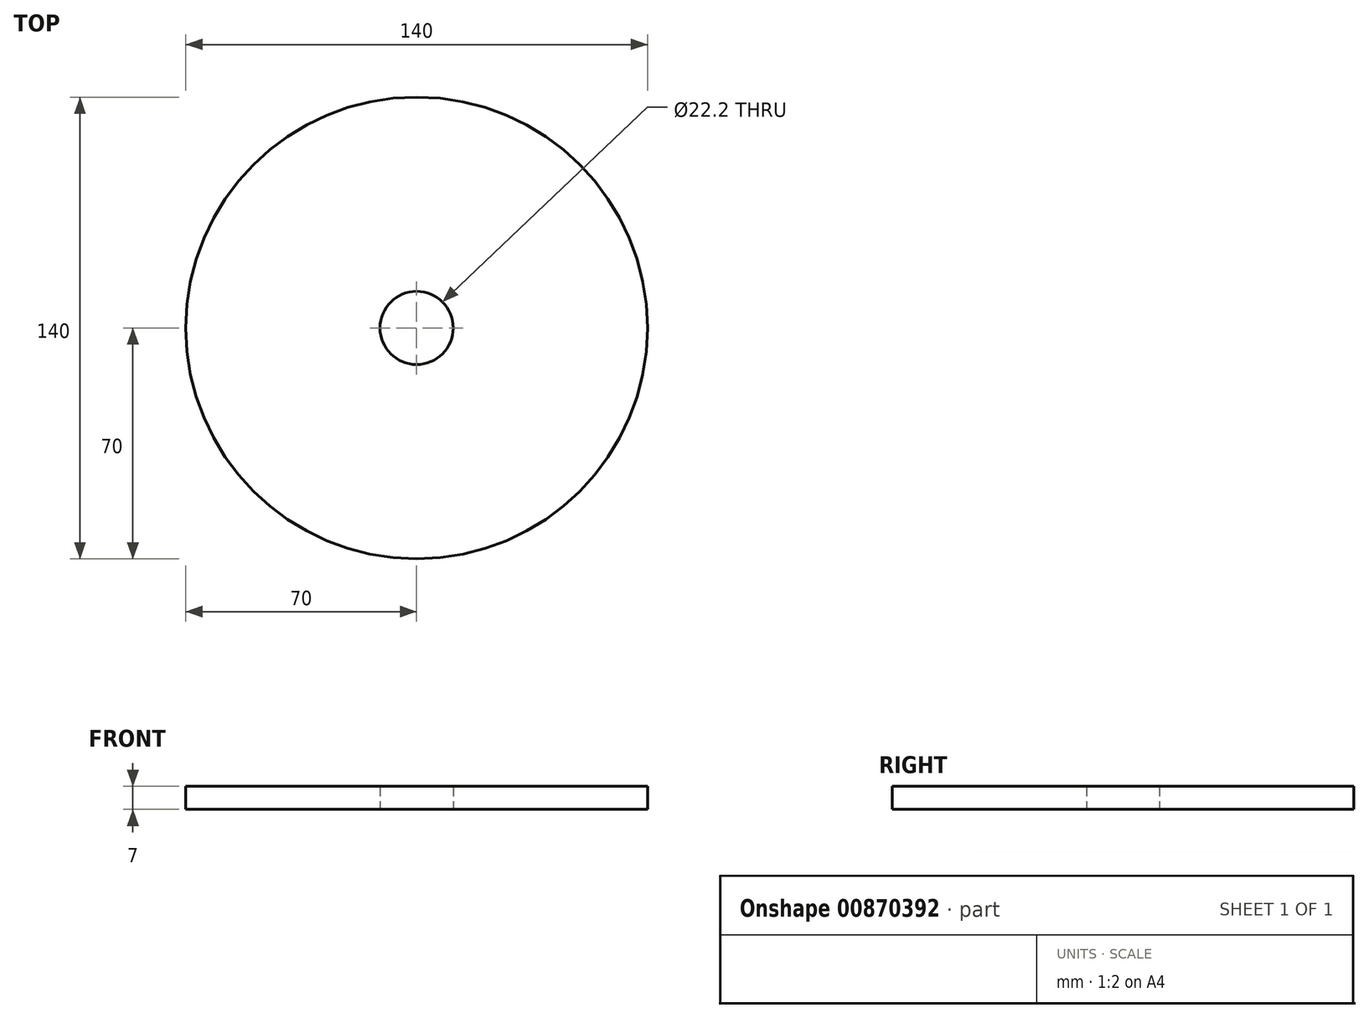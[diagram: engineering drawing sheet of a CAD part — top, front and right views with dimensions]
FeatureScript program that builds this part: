
annotation { "Feature Type Name" : "Feature", "Feature Type Description" : "" }
export const myFeature = defineFeature(function(context is Context, id is Id, definition is map)
    precondition{}
    {
        {
            var Q0;
            Q0=qCreatedBy(makeId("Top.planeOp"),FACE);
            var sketch = newSketch(context, id + "F0", { "sketchPlane" : qUnion([Q0])});
            skCircle(sketch, "E0", {"center": v(0, 0) * mm, "radius": 70 * mm});
            skCircle(sketch, "E1", {"center": v(0, 0) * mm, "radius": 11.1 * mm});
            skSolve(sketch);
        }
        {
            var Q0;
            Q0 = qSketchRegion(id + "F0", true);
            var Q1;
            Q1=makeQuery(id+"F0.imprint","IMPRINT",FACE,{"disambiguationData":[TD([[makeQuery(id+"F0.imprint","IMPRINT",EDGE,{"derivedFrom":sQuery(id+"F0.wireOp",EDGE,"E0")}),1.0]])]});
            extrude(context, id + "F1", {"entities" : qUnion([Q0, Q1]), "depth" : 7 * mm, "offsetDistance" : 25 * mm});
        }
    });
